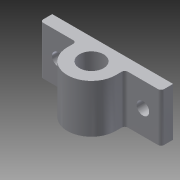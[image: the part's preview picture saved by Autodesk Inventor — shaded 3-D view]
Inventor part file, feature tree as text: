
AUTODESK INVENTOR PART (.ipt)
format: ipt  version: 2013 (Build 170138000, 138)  size: 126,976 bytes
history: native  units: in
note: dims shown in document units (in); Inventor stores cm internally (conversion verified against a paired STEP export)
features: sketch x2, extrude x2, projected_geometry x2, fillet x1
ambient origin geometry x8: Origin, YZ Plane, XZ Plane, XY Plane, X Axis, Y Axis, Z Axis, Center Point
bodies: Solid1 (feature_tree)
feature tree (7):
  sketch  "Sketch1"  dims[d0=1.0in d1=0.9375in d2=0.5in]
  extrude  "Extrusion1"  Depth=0.9375in
  fillet  "Fillet1"  Radius=0.5in
  extrude  "Extrusion3"  Depth=0.25in
  sketch  "Sketch2"  dims[d3=1.0in d4=0.0in d9=0.25in d10=0.75in d11=0.75in d12=0.25in d13=0.5in d14=0.0625in d15=0.26in d16=0.26in d17=0.25in d18=0.0in d20=0.4375in d21=1.75in]
  projected_geometry  "Projected Loop1"
  projected_geometry  "Projected Loop2"
